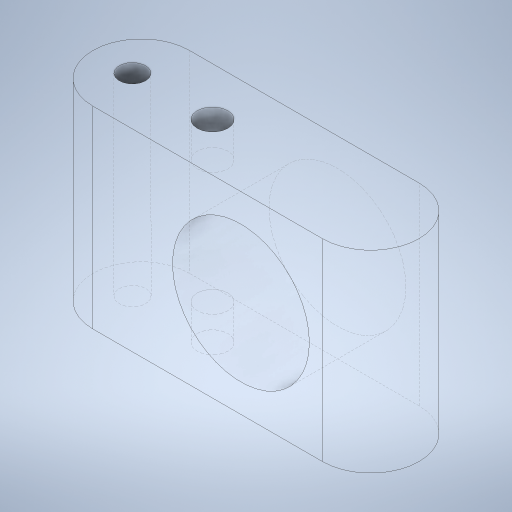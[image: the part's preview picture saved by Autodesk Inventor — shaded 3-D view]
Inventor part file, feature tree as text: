
AUTODESK INVENTOR PART (.ipt)
format: ipt  version: 2023 (Build 270158000, 158)  size: 299,008 bytes
history: native  units: in
note: dims shown in document units (in); Inventor stores cm internally (conversion verified against a paired STEP export)
features: extrude x4, sketch x3, fillet x1
ambient origin geometry x8: Origin, YZ Plane, XZ Plane, XY Plane, X Axis, Y Axis, Z Axis, Center Point
bodies: Solid1 (feature_tree)
feature tree (8):
  extrude  "Extrusion1"  Depth=0.3439in
  sketch  "Sketch2"  dims[d2=0.7033in d3=0.4331in]
  extrude  "Extrusion2"  Depth=0.4331in
  extrude  "Extrusion3"  Depth=0.4331in
  extrude  "Extrusion4"  Depth=0.4331in
  fillet  "Fillet1"  Radius=0.2756in
  sketch  "Sketch1"  dims[d0=0.6142in d1=0.3439in]
  sketch  "Sketch3"  dims[d4=0.4331in d5=0.4331in d6=0.4331in d7=0.2756in d8=0.1772in d9=0.4331in d10=0.0in d11=0.1772in d13=0.3594in d14=0.1181in d15=0.1378in d16=0.4331in d17=0.0in d18=0.1575in d19=0.0in d20=0.1575in d21=0.0in d22=0.2165in d23=1.4632in]
